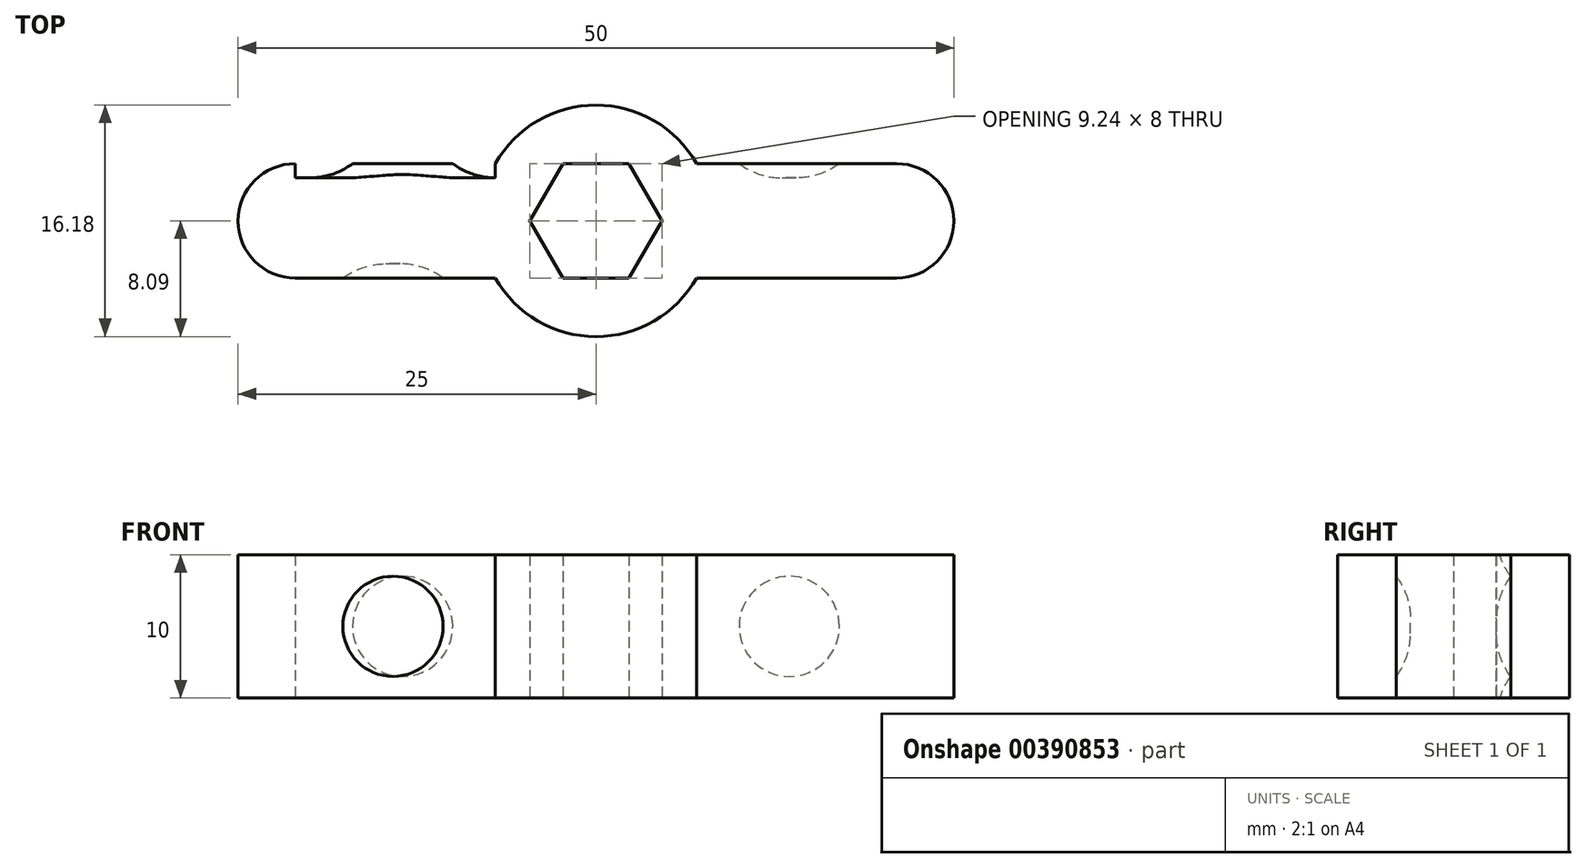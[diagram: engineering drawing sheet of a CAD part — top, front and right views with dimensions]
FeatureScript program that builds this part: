
annotation { "Feature Type Name" : "Feature", "Feature Type Description" : "" }
export const myFeature = defineFeature(function(context is Context, id is Id, definition is map)
    precondition{}
    {
        {
            var Q0;
            Q0=qCreatedBy(makeId("Top.planeOp"),FACE);
            var sketch = newSketch(context, id + "F0", { "sketchPlane" : qUnion([Q0])});
            skCircle(sketch, "E0.cCircle", {"center": v(0, 0) * mm, "radius": 4 * mm, "construction": true});
            skLineSegment(sketch, "E0.0", {"start": v(-2.3, 4) * mm, "end": v(2.3, 4) * mm});
            skLineSegment(sketch, "E0.1", {"start": v(2.3, 4) * mm, "end": v(4.62, 0) * mm});
            skLineSegment(sketch, "E0.2", {"start": v(4.62, 0) * mm, "end": v(2.3, -4) * mm});
            skLineSegment(sketch, "E0.3", {"start": v(2.3, -4) * mm, "end": v(-2.3, -4) * mm});
            skLineSegment(sketch, "E0.4", {"start": v(-2.3, -4) * mm, "end": v(-4.62, 0) * mm});
            skLineSegment(sketch, "E0.5", {"start": v(-4.62, 0) * mm, "end": v(-2.3, 4) * mm});
            skPoint(sketch, "E0.0.midPoint", {"position": v(0, 4) * mm});
            skLineSegment(sketch, "E1", {"start": v(0, 20.7) * mm, "end": v(0, -26.35) * mm, "construction": true});
            skPoint(sketch, "E1.startSnap0", {"position": v(0, 5) * mm});
            skLineSegment(sketch, "E2", {"start": v(40.75, 0) * mm, "end": v(-37.81, 0) * mm, "construction": true});
            skCircle(sketch, "E3", {"center": v(0, 0) * mm, "radius": 8.09 * mm});
            skLineSegment(sketch, "E4.bottom", {"start": v(-21, -4) * mm, "end": v(21, -4) * mm});
            skLineSegment(sketch, "E4.top", {"start": v(-21, 4) * mm, "end": v(21, 4) * mm});
            skLineSegment(sketch, "E4.left", {"start": v(-25, 0) * mm, "end": v(-25, 0) * mm});
            skLineSegment(sketch, "E4.right", {"start": v(25, 0) * mm, "end": v(25, 0) * mm});
            skPoint(sketch, "E5.visualSharp", {"position": v(-25, 4) * mm});
            skArc(sketch, "E5.filletArc", {"start": v(-21, 4) * mm, "mid": v(-23.83, 2.83) * mm, "end": v(-25, 0) * mm});
            skPoint(sketch, "E6.visualSharp", {"position": v(-25, -4) * mm});
            skArc(sketch, "E6.filletArc", {"start": v(-25, 0) * mm, "mid": v(-23.83, -2.83) * mm, "end": v(-21, -4) * mm});
            skPoint(sketch, "E7.visualSharp", {"position": v(25, -4) * mm});
            skArc(sketch, "E7.filletArc", {"start": v(21, -4) * mm, "mid": v(23.83, -2.83) * mm, "end": v(25, 0) * mm});
            skPoint(sketch, "E8.visualSharp", {"position": v(25, 4) * mm});
            skArc(sketch, "E8.filletArc", {"start": v(25, 0) * mm, "mid": v(23.83, 2.83) * mm, "end": v(21, 4) * mm});
            skSolve(sketch);
        }
        {
            var Q0;
            Q0 = qSketchRegion(id + "F0", true);
            extrude(context, id + "F1", {"entities" : qUnion([Q0]), "depth" : 10 * mm, "offsetDistance" : 25 * mm});
        }
        {
            var Q0;
            {var subQ0=sQuery(id+"F0.wireOp",EDGE,"E4.bottom");Q0=makeQuery(id+"F1.opExtrude","SWEPT_FACE",FACE,{"disambiguationData":[OSD([subQ0]),TDD([makeQuery(id+"F0.imprint","IMPRINT",EDGE,{"disambiguationData":[TD([[makeQuery(id+"F0.imprint","INTERSECT",VERTEX,{"derivedFrom":[subQ0,sQuery(id+"F0.wireOp",EDGE,"E6.filletArc")]}),-1.0]])],"derivedFrom":subQ0})])]});}
            var sketch = newSketch(context, id + "F2", { "sketchPlane" : qUnion([Q0])});
            skLineSegment(sketch, "E9", {"start": v(0, -4.1) * mm, "end": v(0, 14.1) * mm, "construction": true});
            skCircle(sketch, "E10", {"center": v(-14.17, 5) * mm, "radius": 3.5 * mm});
            skPoint(sketch, "E10.centerSnap0", {"position": v(0, 5) * mm});
            skLineSegment(sketch, "E11", {"start": v(-14.01, 10) * mm, "end": v(0, 10) * mm, "construction": true});
            skCircle(sketch, "E12.MirrorC", {"center": v(14.17, 5) * mm, "radius": 3.5 * mm});
            skSolve(sketch);
        }
        {
            var Q0;
            {var subQ0=sQuery(id+"F0.wireOp",EDGE,"E4.top");Q0=makeQuery(id+"F1.opExtrude","SWEPT_FACE",FACE,{"disambiguationData":[OSD([subQ0]),TDD([makeQuery(id+"F0.imprint","IMPRINT",EDGE,{"disambiguationData":[TD([[makeQuery(id+"F0.imprint","INTERSECT",VERTEX,{"derivedFrom":[subQ0,sQuery(id+"F0.wireOp",EDGE,"E5.filletArc")]}),-1.0]])],"derivedFrom":subQ0})])]});}
            var sketch = newSketch(context, id + "F3", { "sketchPlane" : qUnion([Q0])});
            skCircle(sketch, "E13", {"center": v(-13.5, 5) * mm, "radius": 3.5 * mm});
            skCircle(sketch, "E14.MirrorC", {"center": v(13.5, 5) * mm, "radius": 3.5 * mm});
            skSolve(sketch);
        }
        {
            var Q0;
            Q0=makeQuery(id+"F2.imprint","IMPRINT",FACE,{"disambiguationData":[TD([[makeQuery(id+"F2.imprint","IMPRINT",EDGE,{"derivedFrom":sQuery(id+"F2.wireOp",EDGE,"E10")}),1.0]])]});
            var Q1;
            Q1=makeQuery(id+"F2.imprint","IMPRINT",FACE,{"disambiguationData":[TD([[makeQuery(id+"F2.imprint","IMPRINT",EDGE,{"derivedFrom":sQuery(id+"F2.wireOp",EDGE,"E12.MirrorC")}),-1.0]])]});
            extrude(context, id + "F4", {"entities" : qUnion([Q0, Q1]), "operationType" : NewBodyOperationType.REMOVE, "oppositeDirection" : true, "depth" : 1 * mm, "offsetDistance" : 25 * mm});
        }
        {
            var Q0;
            Q0=makeQuery(id+"F4.boolean.opBoolean","COPY",EDGE,{"derivedFrom":makeQuery(id+"F4.opExtrude","CAP_EDGE",EDGE,{"disambiguationData":[OSD([sQuery(id+"F2.wireOp",EDGE,"E10")])],"isStart":false})});
            var Q1;
            Q1=makeQuery(id+"F4.boolean.opBoolean","COPY",EDGE,{"derivedFrom":makeQuery(id+"F4.opExtrude","CAP_EDGE",EDGE,{"disambiguationData":[OSD([sQuery(id+"F2.wireOp",EDGE,"E12.MirrorC")])],"isStart":false})});
            fillet(context, id + "F5", {"entities" : qUnion([Q0, Q1]), "radius" : 5 * mm, "tangentPropagation" : true, "allowEdgeOverflow" : false});
        }
        {
            var Q0;
            Q0=makeQuery(id+"F3.imprint","IMPRINT",FACE,{"disambiguationData":[TD([[makeQuery(id+"F3.imprint","IMPRINT",EDGE,{"derivedFrom":sQuery(id+"F3.wireOp",EDGE,"E14.MirrorC")}),-1.0]])]});
            var Q1;
            Q1=makeQuery(id+"F3.imprint","IMPRINT",FACE,{"disambiguationData":[TD([[makeQuery(id+"F3.imprint","IMPRINT",EDGE,{"derivedFrom":sQuery(id+"F3.wireOp",EDGE,"E13")}),1.0]])]});
            extrude(context, id + "F6", {"entities" : qUnion([Q0, Q1]), "operationType" : NewBodyOperationType.REMOVE, "oppositeDirection" : true, "depth" : 1 * mm, "offsetDistance" : 25 * mm});
        }
        {
            var Q0;
            Q0=makeQuery(id+"F6.boolean.opBoolean","COPY",FACE,{"derivedFrom":makeQuery(id+"F6.opExtrude","CAP_FACE",FACE,{"disambiguationData":[OSD([sQuery(id+"F3.wireOp",EDGE,"E13")])],"isStart":false})});
            var Q1;
            Q1=makeQuery(id+"F6.boolean.opBoolean","COPY",EDGE,{"derivedFrom":makeQuery(id+"F6.opExtrude","CAP_EDGE",EDGE,{"disambiguationData":[OSD([sQuery(id+"F3.wireOp",EDGE,"E14.MirrorC")])],"isStart":false})});
            fillet(context, id + "F7", {"entities" : qUnion([Q0, Q1]), "radius" : 5 * mm, "tangentPropagation" : true, "allowEdgeOverflow" : false});
        }
    });
